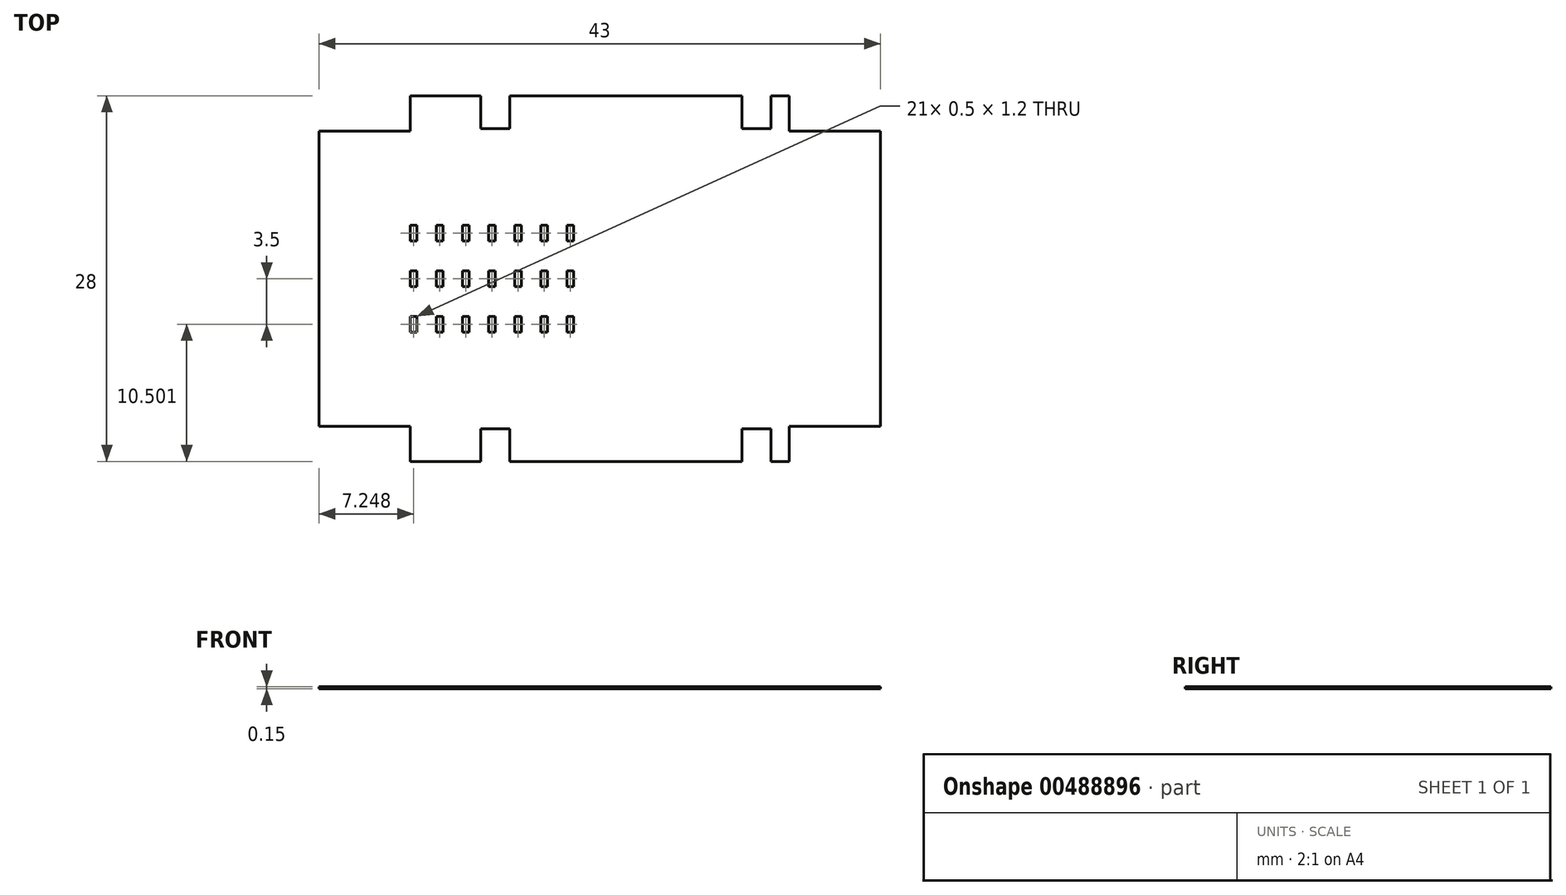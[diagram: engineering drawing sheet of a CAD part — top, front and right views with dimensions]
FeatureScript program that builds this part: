
annotation { "Feature Type Name" : "Feature", "Feature Type Description" : "" }
export const myFeature = defineFeature(function(context is Context, id is Id, definition is map)
    precondition{}
    {
        {
            var Q0;
            Q0=qCreatedBy(makeId("Top.planeOp"),FACE);
            var sketch = newSketch(context, id + "F0", { "sketchPlane" : qUnion([Q0])});
            skLineSegment(sketch, "E0.bottom", {"start": v(32.19, -11.3) * mm, "end": v(25.19, -11.3) * mm});
            skLineSegment(sketch, "E0.top", {"start": v(32.19, 11.3) * mm, "end": v(25.19, 11.3) * mm});
            skLineSegment(sketch, "E0.left", {"start": v(32.19, -11.3) * mm, "end": v(32.19, 11.3) * mm});
            skLineSegment(sketch, "E0.right", {"start": v(-10.81, -11.3) * mm, "end": v(-10.81, 11.3) * mm});
            skPoint(sketch, "E0.middle", {"position": v(10.69, 0) * mm});
            skLineSegment(sketch, "E1.bottom", {"start": v(-3.31, -0.6) * mm, "end": v(-3.81, -0.6) * mm});
            skLineSegment(sketch, "E1.top", {"start": v(-3.31, 0.6) * mm, "end": v(-3.81, 0.6) * mm});
            skLineSegment(sketch, "E1.left", {"start": v(-3.31, -0.6) * mm, "end": v(-3.31, 0.6) * mm});
            skLineSegment(sketch, "E1.right", {"start": v(-3.81, -0.6) * mm, "end": v(-3.81, 0.6) * mm});
            skLineSegment(sketch, "E2.1.0.0", {"start": v(-1.31, -0.6) * mm, "end": v(-1.81, -0.6) * mm});
            skLineSegment(sketch, "E2.1.0.1", {"start": v(-1.31, 0.6) * mm, "end": v(-1.81, 0.6) * mm});
            skLineSegment(sketch, "E2.1.0.2", {"start": v(-1.81, -0.6) * mm, "end": v(-1.81, 0.6) * mm});
            skLineSegment(sketch, "E2.1.0.3", {"start": v(-1.31, -0.6) * mm, "end": v(-1.31, 0.6) * mm});
            skLineSegment(sketch, "E2.2.0.0", {"start": v(0.69, -0.6) * mm, "end": v(0.19, -0.6) * mm});
            skLineSegment(sketch, "E2.2.0.1", {"start": v(0.69, 0.6) * mm, "end": v(0.19, 0.6) * mm});
            skLineSegment(sketch, "E2.2.0.2", {"start": v(0.19, -0.6) * mm, "end": v(0.19, 0.6) * mm});
            skLineSegment(sketch, "E2.2.0.3", {"start": v(0.69, -0.6) * mm, "end": v(0.69, 0.6) * mm});
            skLineSegment(sketch, "E2.3.0.0", {"start": v(2.69, -0.6) * mm, "end": v(2.19, -0.6) * mm});
            skLineSegment(sketch, "E2.3.0.1", {"start": v(2.69, 0.6) * mm, "end": v(2.19, 0.6) * mm});
            skLineSegment(sketch, "E2.3.0.2", {"start": v(2.19, -0.6) * mm, "end": v(2.19, 0.6) * mm});
            skLineSegment(sketch, "E2.3.0.3", {"start": v(2.69, -0.6) * mm, "end": v(2.69, 0.6) * mm});
            skLineSegment(sketch, "E2.4.0.0", {"start": v(4.69, -0.6) * mm, "end": v(4.19, -0.6) * mm});
            skLineSegment(sketch, "E2.4.0.1", {"start": v(4.69, 0.6) * mm, "end": v(4.19, 0.6) * mm});
            skLineSegment(sketch, "E2.4.0.2", {"start": v(4.19, -0.6) * mm, "end": v(4.19, 0.6) * mm});
            skLineSegment(sketch, "E2.4.0.3", {"start": v(4.69, -0.6) * mm, "end": v(4.69, 0.6) * mm});
            skLineSegment(sketch, "E2.5.0.0", {"start": v(6.69, -0.6) * mm, "end": v(6.19, -0.6) * mm});
            skLineSegment(sketch, "E2.5.0.1", {"start": v(6.69, 0.6) * mm, "end": v(6.19, 0.6) * mm});
            skLineSegment(sketch, "E2.5.0.2", {"start": v(6.19, -0.6) * mm, "end": v(6.19, 0.6) * mm});
            skLineSegment(sketch, "E2.5.0.3", {"start": v(6.69, -0.6) * mm, "end": v(6.69, 0.6) * mm});
            skLineSegment(sketch, "E2.6.0.0", {"start": v(8.69, -0.6) * mm, "end": v(8.19, -0.6) * mm});
            skLineSegment(sketch, "E2.6.0.1", {"start": v(8.69, 0.6) * mm, "end": v(8.19, 0.6) * mm});
            skLineSegment(sketch, "E2.6.0.2", {"start": v(8.19, -0.6) * mm, "end": v(8.19, 0.6) * mm});
            skLineSegment(sketch, "E2.6.0.3", {"start": v(8.69, -0.6) * mm, "end": v(8.69, 0.6) * mm});
            skLineSegment(sketch, "E2.direction1", {"start": v(-3.81, -0.6) * mm, "end": v(-1.81, -0.6) * mm, "construction": true});
            skLineSegment(sketch, "E3.1.0.0", {"start": v(0.69, -4.1) * mm, "end": v(0.19, -4.1) * mm});
            skLineSegment(sketch, "E3.1.0.1", {"start": v(-3.81, -4.1) * mm, "end": v(-1.81, -4.1) * mm, "construction": true});
            skLineSegment(sketch, "E3.1.0.2", {"start": v(6.69, -4.1) * mm, "end": v(6.19, -4.1) * mm});
            skLineSegment(sketch, "E3.1.0.3", {"start": v(6.69, -2.9) * mm, "end": v(6.19, -2.9) * mm});
            skLineSegment(sketch, "E3.1.0.4", {"start": v(4.69, -4.1) * mm, "end": v(4.69, -2.9) * mm});
            skLineSegment(sketch, "E3.1.0.5", {"start": v(0.69, -4.1) * mm, "end": v(0.69, -2.9) * mm});
            skLineSegment(sketch, "E3.1.0.6", {"start": v(0.19, -4.1) * mm, "end": v(0.19, -2.9) * mm});
            skLineSegment(sketch, "E3.1.0.7", {"start": v(0.69, -2.9) * mm, "end": v(0.19, -2.9) * mm});
            skLineSegment(sketch, "E3.1.0.8", {"start": v(8.69, -4.1) * mm, "end": v(8.69, -2.9) * mm});
            skLineSegment(sketch, "E3.1.0.9", {"start": v(4.19, -4.1) * mm, "end": v(4.19, -2.9) * mm});
            skLineSegment(sketch, "E3.1.0.10", {"start": v(8.19, -4.1) * mm, "end": v(8.19, -2.9) * mm});
            skLineSegment(sketch, "E3.1.0.11", {"start": v(4.69, -2.9) * mm, "end": v(4.19, -2.9) * mm});
            skLineSegment(sketch, "E3.1.0.12", {"start": v(8.69, -4.1) * mm, "end": v(8.19, -4.1) * mm});
            skLineSegment(sketch, "E3.1.0.13", {"start": v(8.69, -2.9) * mm, "end": v(8.19, -2.9) * mm});
            skLineSegment(sketch, "E3.1.0.14", {"start": v(4.69, -4.1) * mm, "end": v(4.19, -4.1) * mm});
            skLineSegment(sketch, "E3.1.0.15", {"start": v(6.69, -4.1) * mm, "end": v(6.69, -2.9) * mm});
            skLineSegment(sketch, "E3.1.0.16", {"start": v(6.19, -4.1) * mm, "end": v(6.19, -2.9) * mm});
            skLineSegment(sketch, "E3.1.0.17", {"start": v(2.69, -2.9) * mm, "end": v(2.19, -2.9) * mm});
            skLineSegment(sketch, "E3.1.0.18", {"start": v(2.69, -4.1) * mm, "end": v(2.19, -4.1) * mm});
            skLineSegment(sketch, "E3.1.0.19", {"start": v(-1.81, -4.1) * mm, "end": v(-1.81, -2.9) * mm});
            skLineSegment(sketch, "E3.1.0.20", {"start": v(-1.31, -4.1) * mm, "end": v(-1.31, -2.9) * mm});
            skLineSegment(sketch, "E3.1.0.21", {"start": v(2.19, -4.1) * mm, "end": v(2.19, -2.9) * mm});
            skLineSegment(sketch, "E3.1.0.22", {"start": v(-1.31, -4.1) * mm, "end": v(-1.81, -4.1) * mm});
            skLineSegment(sketch, "E3.1.0.23", {"start": v(-3.81, -4.1) * mm, "end": v(-3.81, -2.9) * mm});
            skLineSegment(sketch, "E3.1.0.24", {"start": v(-3.31, -4.1) * mm, "end": v(-3.31, -2.9) * mm});
            skLineSegment(sketch, "E3.1.0.25", {"start": v(-3.31, -2.9) * mm, "end": v(-3.81, -2.9) * mm});
            skLineSegment(sketch, "E3.1.0.26", {"start": v(-3.31, -4.1) * mm, "end": v(-3.81, -4.1) * mm});
            skLineSegment(sketch, "E3.1.0.27", {"start": v(2.69, -4.1) * mm, "end": v(2.69, -2.9) * mm});
            skLineSegment(sketch, "E3.1.0.28", {"start": v(-1.31, -2.9) * mm, "end": v(-1.81, -2.9) * mm});
            skLineSegment(sketch, "E3.direction1", {"start": v(-3.81, -0.6) * mm, "end": v(-3.81, -4.1) * mm, "construction": true});
            skLineSegment(sketch, "E4.1.0.0", {"start": v(6.69, 2.9) * mm, "end": v(6.69, 4.1) * mm});
            skLineSegment(sketch, "E4.1.0.1", {"start": v(4.19, 2.9) * mm, "end": v(4.19, 4.1) * mm});
            skLineSegment(sketch, "E4.1.0.2", {"start": v(8.19, 2.9) * mm, "end": v(8.19, 4.1) * mm});
            skLineSegment(sketch, "E4.1.0.3", {"start": v(2.19, 2.9) * mm, "end": v(2.19, 4.1) * mm});
            skLineSegment(sketch, "E4.1.0.4", {"start": v(-3.81, 2.9) * mm, "end": v(-1.81, 2.9) * mm, "construction": true});
            skLineSegment(sketch, "E4.1.0.5", {"start": v(4.69, 2.9) * mm, "end": v(4.69, 4.1) * mm});
            skLineSegment(sketch, "E4.1.0.6", {"start": v(-1.31, 2.9) * mm, "end": v(-1.31, 4.1) * mm});
            skLineSegment(sketch, "E4.1.0.7", {"start": v(-1.81, 2.9) * mm, "end": v(-1.81, 4.1) * mm});
            skLineSegment(sketch, "E4.1.0.8", {"start": v(-3.81, 2.9) * mm, "end": v(-3.81, 4.1) * mm});
            skLineSegment(sketch, "E4.1.0.9", {"start": v(-3.31, 2.9) * mm, "end": v(-3.31, 4.1) * mm});
            skLineSegment(sketch, "E4.1.0.10", {"start": v(6.19, 2.9) * mm, "end": v(6.19, 4.1) * mm});
            skLineSegment(sketch, "E4.1.0.11", {"start": v(2.69, 2.9) * mm, "end": v(2.69, 4.1) * mm});
            skLineSegment(sketch, "E4.1.0.12", {"start": v(0.69, 2.9) * mm, "end": v(0.69, 4.1) * mm});
            skLineSegment(sketch, "E4.1.0.13", {"start": v(0.19, 2.9) * mm, "end": v(0.19, 4.1) * mm});
            skLineSegment(sketch, "E4.1.0.14", {"start": v(8.69, 2.9) * mm, "end": v(8.69, 4.1) * mm});
            skLineSegment(sketch, "E4.1.0.15", {"start": v(2.69, 4.1) * mm, "end": v(2.19, 4.1) * mm});
            skLineSegment(sketch, "E4.1.0.16", {"start": v(4.69, 2.9) * mm, "end": v(4.19, 2.9) * mm});
            skLineSegment(sketch, "E4.1.0.17", {"start": v(4.69, 4.1) * mm, "end": v(4.19, 4.1) * mm});
            skLineSegment(sketch, "E4.1.0.18", {"start": v(8.69, 4.1) * mm, "end": v(8.19, 4.1) * mm});
            skLineSegment(sketch, "E4.1.0.19", {"start": v(6.69, 4.1) * mm, "end": v(6.19, 4.1) * mm});
            skLineSegment(sketch, "E4.1.0.20", {"start": v(6.69, 2.9) * mm, "end": v(6.19, 2.9) * mm});
            skLineSegment(sketch, "E4.1.0.21", {"start": v(8.69, 2.9) * mm, "end": v(8.19, 2.9) * mm});
            skLineSegment(sketch, "E4.1.0.22", {"start": v(2.69, 2.9) * mm, "end": v(2.19, 2.9) * mm});
            skLineSegment(sketch, "E4.1.0.23", {"start": v(0.69, 2.9) * mm, "end": v(0.19, 2.9) * mm});
            skLineSegment(sketch, "E4.1.0.24", {"start": v(-1.31, 4.1) * mm, "end": v(-1.81, 4.1) * mm});
            skLineSegment(sketch, "E4.1.0.25", {"start": v(-1.31, 2.9) * mm, "end": v(-1.81, 2.9) * mm});
            skLineSegment(sketch, "E4.1.0.26", {"start": v(-3.31, 4.1) * mm, "end": v(-3.81, 4.1) * mm});
            skLineSegment(sketch, "E4.1.0.27", {"start": v(-3.31, 2.9) * mm, "end": v(-3.81, 2.9) * mm});
            skLineSegment(sketch, "E4.1.0.28", {"start": v(0.69, 4.1) * mm, "end": v(0.19, 4.1) * mm});
            skLineSegment(sketch, "E4.direction1", {"start": v(-3.81, -0.6) * mm, "end": v(-3.81, 2.9) * mm, "construction": true});
            skLineSegment(sketch, "E5.bottom", {"start": v(25.19, -14) * mm, "end": v(23.79, -14) * mm});
            skLineSegment(sketch, "E5.top", {"start": v(25.19, 14) * mm, "end": v(23.79, 14) * mm});
            skLineSegment(sketch, "E5.left", {"start": v(25.19, -14) * mm, "end": v(25.19, -11.3) * mm});
            skLineSegment(sketch, "E5.right", {"start": v(-3.81, -14) * mm, "end": v(-3.81, -11.3) * mm});
            skLineSegment(sketch, "E6.top", {"start": v(1.59, 11.5) * mm, "end": v(3.79, 11.5) * mm});
            skLineSegment(sketch, "E6.left", {"start": v(1.59, 14) * mm, "end": v(1.59, 11.5) * mm});
            skLineSegment(sketch, "E6.right", {"start": v(3.79, 14) * mm, "end": v(3.79, 11.5) * mm});
            skLineSegment(sketch, "E7.top", {"start": v(21.59, 11.5) * mm, "end": v(23.79, 11.5) * mm});
            skLineSegment(sketch, "E7.left", {"start": v(21.59, 14) * mm, "end": v(21.59, 11.5) * mm});
            skLineSegment(sketch, "E7.right", {"start": v(23.79, 14) * mm, "end": v(23.79, 11.5) * mm});
            skLineSegment(sketch, "E8.MirrorCS", {"start": v(21.59, -14) * mm, "end": v(21.59, -11.5) * mm});
            skLineSegment(sketch, "E9.MirrorCS", {"start": v(1.59, -11.5) * mm, "end": v(3.79, -11.5) * mm});
            skLineSegment(sketch, "E10.MirrorCS", {"start": v(3.79, -14) * mm, "end": v(3.79, -11.5) * mm});
            skLineSegment(sketch, "E11.MirrorCS", {"start": v(21.59, -11.5) * mm, "end": v(23.79, -11.5) * mm});
            skLineSegment(sketch, "E12.MirrorCS", {"start": v(23.79, -14) * mm, "end": v(23.79, -11.5) * mm});
            skLineSegment(sketch, "E13.MirrorCS", {"start": v(1.59, -14) * mm, "end": v(1.59, -11.5) * mm});
            skLineSegment(sketch, "E14.trimOffspring", {"start": v(-3.81, 11.3) * mm, "end": v(-10.81, 11.3) * mm});
            skLineSegment(sketch, "E15.trimOffspring", {"start": v(1.59, 14) * mm, "end": v(-3.81, 14) * mm});
            skLineSegment(sketch, "E16.trimOffspring", {"start": v(21.59, 14) * mm, "end": v(3.79, 14) * mm});
            skLineSegment(sketch, "E17.trimOffspring", {"start": v(-3.81, -11.3) * mm, "end": v(-10.81, -11.3) * mm});
            skLineSegment(sketch, "E18.trimOffspring", {"start": v(1.59, -14) * mm, "end": v(-3.81, -14) * mm});
            skLineSegment(sketch, "E19.trimOffspring", {"start": v(21.59, -14) * mm, "end": v(3.79, -14) * mm});
            skLineSegment(sketch, "E20.trimOffspring", {"start": v(25.19, 11.3) * mm, "end": v(25.19, 14) * mm});
            skLineSegment(sketch, "E21.trimOffspring", {"start": v(-3.81, 11.3) * mm, "end": v(-3.81, 14) * mm});
            skSolve(sketch);
        }
        {
            var Q0;
            Q0=makeQuery(id+"F0.imprint","IMPRINT",FACE,{"disambiguationData":[TD([[makeQuery(id+"F0.imprint","IMPRINT",EDGE,{"derivedFrom":sQuery(id+"F0.wireOp",EDGE,"E0.bottom")}),-1.0]])]});
            extrude(context, id + "F1", {"entities" : qUnion([Q0]), "depth" : 0.15 * mm});
        }
    });
